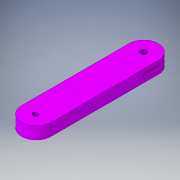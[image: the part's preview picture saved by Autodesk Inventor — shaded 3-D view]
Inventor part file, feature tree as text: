
AUTODESK INVENTOR PART (.ipt)
format: ipt  version: 2017 (Build 210142000, 142)  size: 141,824 bytes
history: native  units: in
note: dims shown in document units (in); Inventor stores cm internally (conversion verified against a paired STEP export)
features: extrude x3, sketch x3
ambient origin geometry x8: Origin, YZ Plane, XZ Plane, XY Plane, X Axis, Y Axis, Z Axis, Center Point
bodies: Solid1 (feature_tree)
feature tree (6):
  extrude  "Extrusion1"  Depth=0.75in
  extrude  "Extrusion2"  TaperAngle=0.0deg  [1 undecoded]
  extrude  "Extrusion3"  Depth=1.5in
  sketch  "Sketch1"  dims[d0=1.5in d2=0.75in]
  sketch  "Sketch2"  dims[d4=0.3125in d6=0.0in]
  sketch  "Sketch3"  dims[d7=0.25in d8=1.5in d9=0.3937in d10=0.0in d11=0.25in d12=1.0in d13=0.0in]
note: 1 required parameter value undecoded (feature->parameter linkage not recoverable at this tier; creation-order binding heuristic only, values carry confidence <= 0.55)
